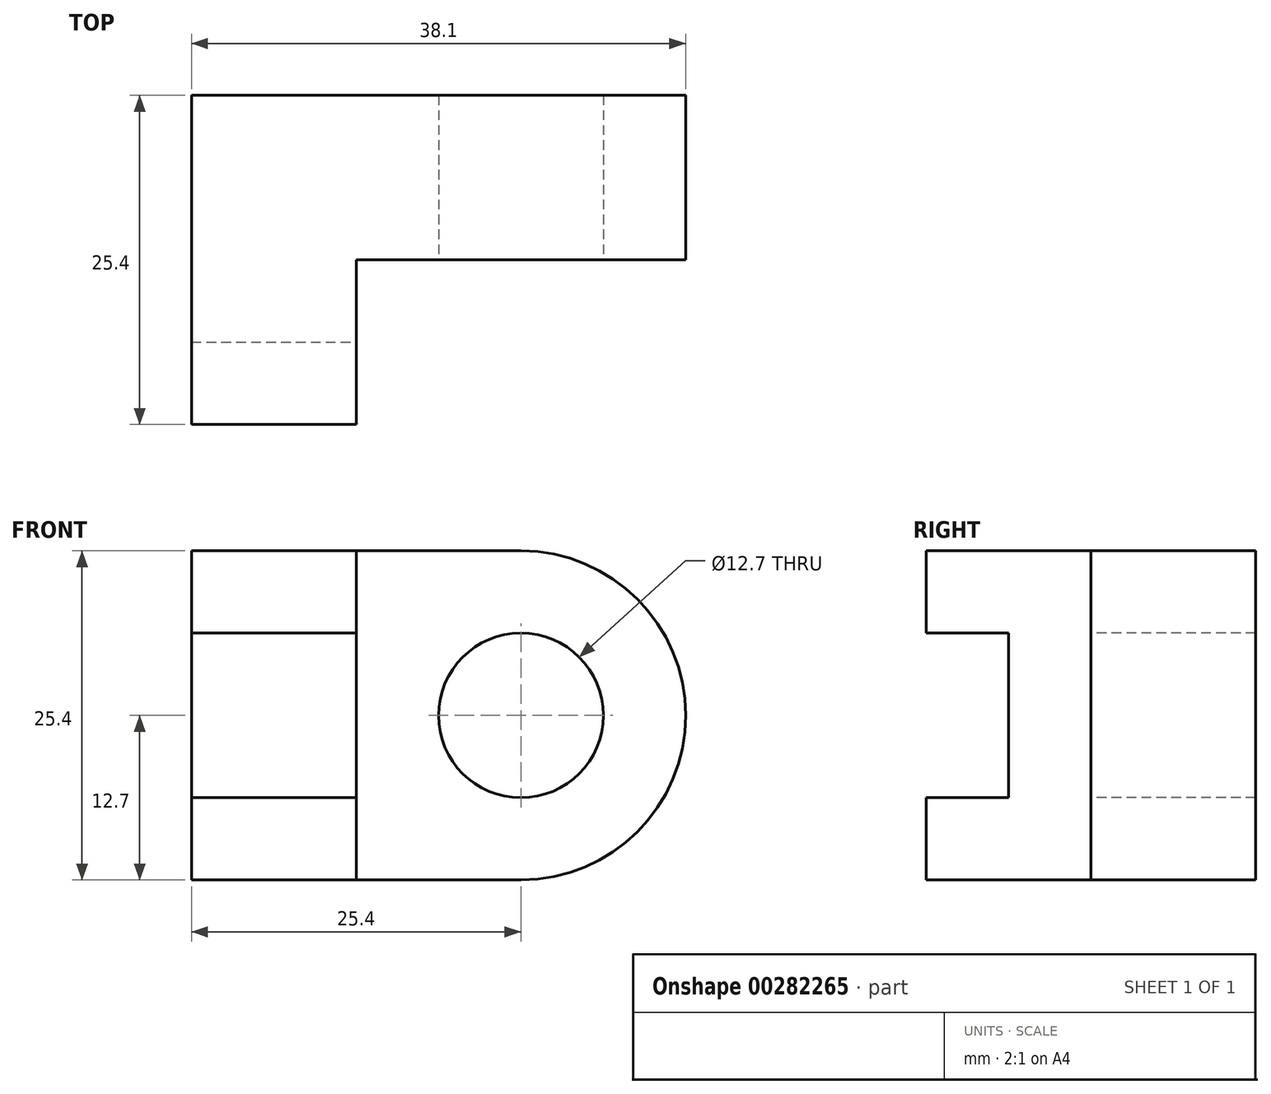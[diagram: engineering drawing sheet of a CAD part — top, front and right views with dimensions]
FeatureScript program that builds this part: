
annotation { "Feature Type Name" : "Feature", "Feature Type Description" : "" }
export const myFeature = defineFeature(function(context is Context, id is Id, definition is map)
    precondition{}
    {
        {
            var Q0;
            Q0=qCreatedBy(makeId("Front.planeOp"),FACE);
            var sketch = newSketch(context, id + "F0", { "sketchPlane" : qUnion([Q0])});
            skLineSegment(sketch, "E0.bottom", {"start": v(0, 0) * mm, "end": v(38.1, 0) * mm});
            skLineSegment(sketch, "E0.top", {"start": v(0, 25.4) * mm, "end": v(38.1, 25.4) * mm});
            skLineSegment(sketch, "E0.left", {"start": v(0, 0) * mm, "end": v(0, 25.4) * mm});
            skLineSegment(sketch, "E0.right", {"start": v(38.1, 0) * mm, "end": v(38.1, 25.4) * mm});
            skSolve(sketch);
        }
        {
            var Q0;
            Q0 = qSketchRegion(id + "F0", true);
            extrude(context, id + "F1", {"entities" : qUnion([Q0]), "depth" : 25.4 * mm});
        }
        {
            var Q0;
            Q0=makeQuery(id+"F1.opExtrude","SWEPT_FACE",FACE,{"disambiguationData":[OSD([sQuery(id+"F0.wireOp",EDGE,"E0.right")])]});
            var sketch = newSketch(context, id + "F2", { "sketchPlane" : qUnion([Q0])});
            skLineSegment(sketch, "E1.bottom", {"start": v(-25.4, 25.4) * mm, "end": v(-12.7, 25.4) * mm});
            skLineSegment(sketch, "E1.top", {"start": v(-25.4, 0) * mm, "end": v(-12.7, 0) * mm});
            skLineSegment(sketch, "E1.left", {"start": v(-25.4, 25.4) * mm, "end": v(-25.4, 0) * mm});
            skLineSegment(sketch, "E1.right", {"start": v(-12.7, 25.4) * mm, "end": v(-12.7, 0) * mm});
            skSolve(sketch);
        }
        {
            var Q0;
            Q0 = qSketchRegion(id + "F2", true);
            extrude(context, id + "F3", {"entities" : qUnion([Q0]), "operationType" : NewBodyOperationType.REMOVE, "oppositeDirection" : true, "depth" : 25.4 * mm});
        }
        {
            var Q0;
            Q0=makeQuery(id+"F1.opExtrude","CAP_FACE",FACE,{"disambiguationData":[OSD([sQuery(id+"F0.wireOp",EDGE,"E0.bottom"),sQuery(id+"F0.wireOp",EDGE,"E0.top"),sQuery(id+"F0.wireOp",EDGE,"E0.left"),sQuery(id+"F0.wireOp",EDGE,"E0.right")])],"isStart":false});
            var sketch = newSketch(context, id + "F4", { "sketchPlane" : qUnion([Q0])});
            skLineSegment(sketch, "E2.bottom", {"start": v(0, 19.05) * mm, "end": v(12.7, 19.05) * mm});
            skLineSegment(sketch, "E2.top", {"start": v(0, 6.35) * mm, "end": v(12.7, 6.35) * mm});
            skLineSegment(sketch, "E2.left", {"start": v(0, 19.05) * mm, "end": v(0, 6.35) * mm});
            skLineSegment(sketch, "E2.right", {"start": v(12.7, 19.05) * mm, "end": v(12.7, 6.35) * mm});
            skSolve(sketch);
        }
        {
            var Q0;
            Q0 = qSketchRegion(id + "F4", true);
            extrude(context, id + "F5", {"entities" : qUnion([Q0]), "operationType" : NewBodyOperationType.REMOVE, "oppositeDirection" : true, "depth" : 6.35 * mm});
        }
        {
            var Q0;
            Q0=makeQuery(id+"F3.boolean.opBoolean","COPY",FACE,{"derivedFrom":makeQuery(id+"F3.opExtrude","SWEPT_FACE",FACE,{"disambiguationData":[OSD([sQuery(id+"F2.wireOp",EDGE,"E1.right")])]})});
            var sketch = newSketch(context, id + "F6", { "sketchPlane" : qUnion([Q0])});
            skLineSegment(sketch, "E3", {"start": v(12.7, 25.4) * mm, "end": v(25.4, 25.4) * mm, "construction": true});
            skArc(sketch, "E4", {"start": v(25.4, 0) * mm, "mid": v(38.1, 12.7) * mm, "end": v(25.4, 25.4) * mm});
            skSolve(sketch);
        }
        {
            var Q0;
            {var subQ0=sQuery(id+"F6.wireOp",EDGE,"E4");var subQ1=sQuery(id+"F2.wireOp",EDGE,"E1.right");var subQ4=makeQuery(id+"F3.boolean.opBoolean","COPY",EDGE,{"derivedFrom":makeQuery(id+"F3.opExtrude","CAP_EDGE",EDGE,{"disambiguationData":[OSD([subQ1])],"isStart":true})});var subQ5=makeQuery(id+"F6.imprint","INTERSECT",VERTEX,{"derivedFrom":[subQ4,subQ0]});Q0=makeQuery(id+"F6.imprint","IMPRINT",FACE,{"disambiguationData":[TD([[makeQuery(id+"F6.imprint","IMPRINT",EDGE,{"disambiguationData":[TD([[subQ5,-1.0]])],"derivedFrom":subQ0}),-1.0]])]});}
            var Q1;
            {var subQ0=sQuery(id+"F6.wireOp",EDGE,"E4");var subQ1=sQuery(id+"F2.wireOp",EDGE,"E1.right");var subQ4=makeQuery(id+"F3.boolean.opBoolean","COPY",EDGE,{"derivedFrom":makeQuery(id+"F3.opExtrude","CAP_EDGE",EDGE,{"disambiguationData":[OSD([subQ1])],"isStart":true})});var subQ5=makeQuery(id+"F6.imprint","INTERSECT",VERTEX,{"derivedFrom":[subQ4,subQ0]});Q1=makeQuery(id+"F6.imprint","IMPRINT",FACE,{"disambiguationData":[TD([[makeQuery(id+"F6.imprint","IMPRINT",EDGE,{"disambiguationData":[TD([[subQ5,1.0]])],"derivedFrom":subQ0}),-1.0]])]});}
            extrude(context, id + "F7", {"entities" : qUnion([Q0, Q1]), "operationType" : NewBodyOperationType.REMOVE, "endBound" : BoundingType.THROUGH_ALL, "oppositeDirection" : true, "depth" : 25.4 * mm});
        }
        {
            var Q0;
            Q0=makeQuery(id+"F3.boolean.opBoolean","COPY",FACE,{"derivedFrom":makeQuery(id+"F3.opExtrude","SWEPT_FACE",FACE,{"disambiguationData":[OSD([sQuery(id+"F2.wireOp",EDGE,"E1.right")])]})});
            var sketch = newSketch(context, id + "F8", { "sketchPlane" : qUnion([Q0])});
            skCircle(sketch, "E5", {"center": v(25.4, 12.7) * mm, "radius": 6.35 * mm});
            skLineSegment(sketch, "E6", {"start": v(12.7, 12.7) * mm, "end": v(19.05, 12.7) * mm, "construction": true});
            skLineSegment(sketch, "E7", {"start": v(25.4, 25.4) * mm, "end": v(25.4, 19.05) * mm, "construction": true});
            skLineSegment(sketch, "E8", {"start": v(25.4, 6.35) * mm, "end": v(25.4, 0) * mm, "construction": true});
            skLineSegment(sketch, "E9", {"start": v(31.75, 12.7) * mm, "end": v(38.1, 12.7) * mm, "construction": true});
            skSolve(sketch);
        }
        {
            var Q0;
            Q0 = qSketchRegion(id + "F8", true);
            extrude(context, id + "F9", {"entities" : qUnion([Q0]), "operationType" : NewBodyOperationType.REMOVE, "endBound" : BoundingType.THROUGH_ALL, "oppositeDirection" : true, "depth" : 25.4 * mm});
        }
    });
